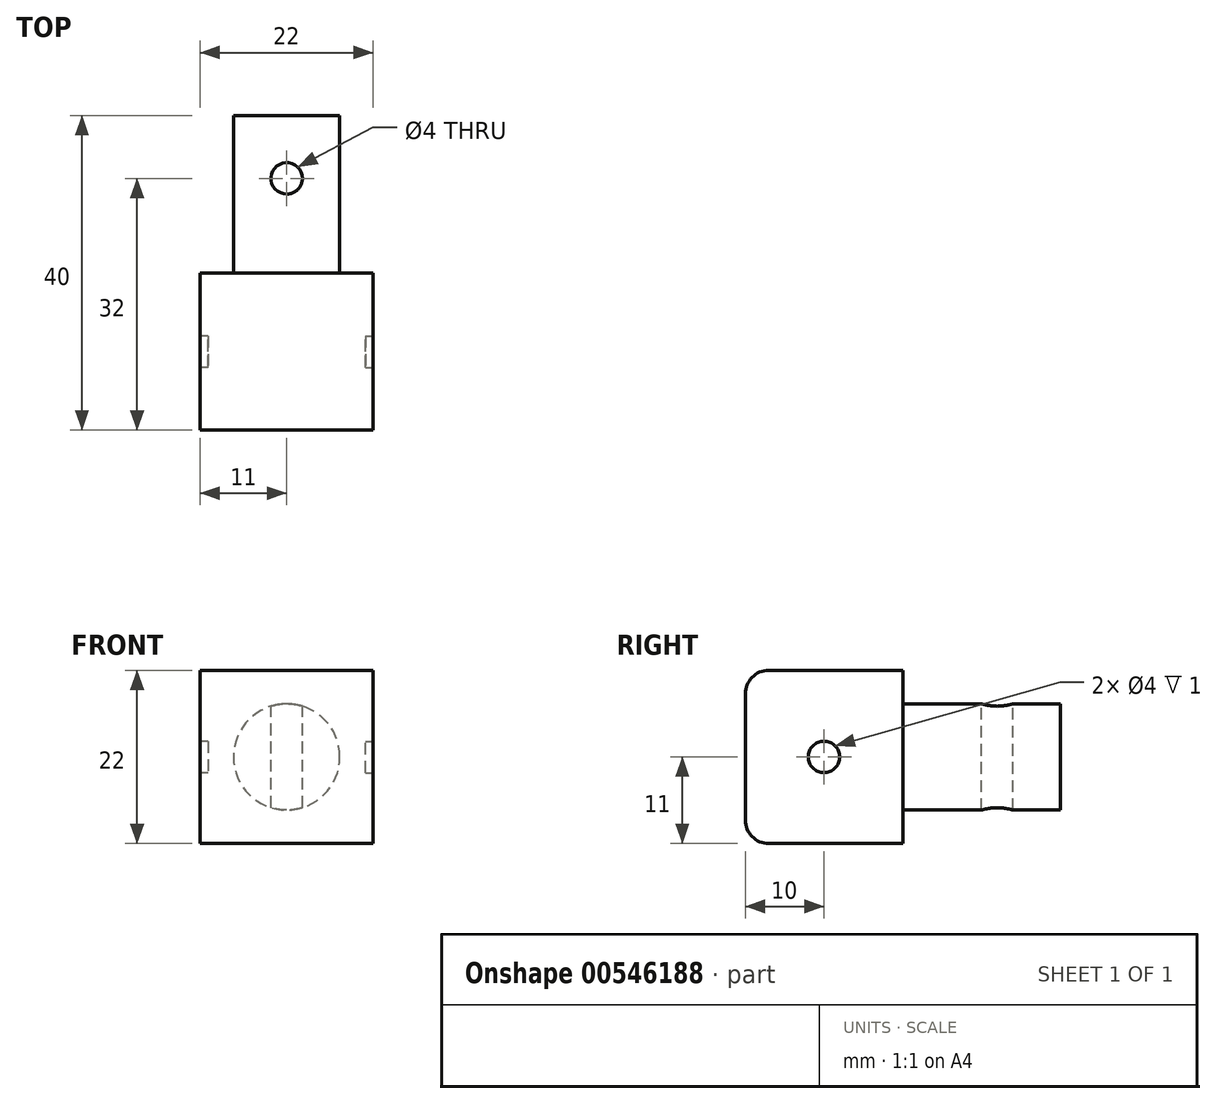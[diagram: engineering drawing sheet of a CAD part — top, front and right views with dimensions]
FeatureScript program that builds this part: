
annotation { "Feature Type Name" : "Feature", "Feature Type Description" : "" }
export const myFeature = defineFeature(function(context is Context, id is Id, definition is map)
    precondition{}
    {
        {
            var Q0;
            Q0=qCreatedBy(makeId("Front.planeOp"),FACE);
            var sketch = newSketch(context, id + "F0", { "sketchPlane" : qUnion([Q0])});
            skCircle(sketch, "E0", {"center": v(0, 0) * mm, "radius": 6.75 * mm});
            skSolve(sketch);
        }
        {
            var Q0;
            Q0 = qSketchRegion(id + "F0", true);
            extrude(context, id + "F1", {"entities" : qUnion([Q0]), "depth" : 20 * mm, "offsetDistance" : 25 * mm});
        }
        {
            var Q0;
            Q0=makeQuery(id+"F1.opExtrude","CAP_FACE",FACE,{"disambiguationData":[OSD([sQuery(id+"F0.wireOp",EDGE,"E0")])],"isStart":false});
            var sketch = newSketch(context, id + "F2", { "sketchPlane" : qUnion([Q0])});
            skLineSegment(sketch, "E1.bottom", {"start": v(-11, 11) * mm, "end": v(11, 11) * mm});
            skLineSegment(sketch, "E1.top", {"start": v(-11, -11) * mm, "end": v(11, -11) * mm});
            skLineSegment(sketch, "E1.left", {"start": v(-11, 11) * mm, "end": v(-11, -11) * mm});
            skLineSegment(sketch, "E1.right", {"start": v(11, 11) * mm, "end": v(11, -11) * mm});
            skPoint(sketch, "E1.middle", {"position": v(0, 0) * mm});
            skSolve(sketch);
        }
        {
            var Q0;
            Q0 = qSketchRegion(id + "F2", true);
            extrude(context, id + "F3", {"entities" : qUnion([Q0]), "operationType" : NewBodyOperationType.ADD, "depth" : 20 * mm, "offsetDistance" : 25 * mm});
        }
        {
            var Q0;
            Q0=makeQuery(id+"F3.opExtrude","CAP_EDGE",EDGE,{"disambiguationData":[OSD([sQuery(id+"F2.wireOp",EDGE,"E1.bottom")])],"isStart":false});
            var Q1;
            Q1=makeQuery(id+"F3.opExtrude","CAP_EDGE",EDGE,{"disambiguationData":[OSD([sQuery(id+"F2.wireOp",EDGE,"E1.top")])],"isStart":false});
            fillet(context, id + "F4", {"entities" : qUnion([Q0, Q1]), "radius" : 3 * mm, "tangentPropagation" : true, "allowEdgeOverflow" : false});
        }
        {
            var Q0;
            Q0=makeQuery(id+"F3.opExtrude","SWEPT_FACE",FACE,{"disambiguationData":[OSD([sQuery(id+"F2.wireOp",EDGE,"E1.right")])]});
            var sketch = newSketch(context, id + "F5", { "sketchPlane" : qUnion([Q0])});
            skLineSegment(sketch, "E2", {"start": v(-40, 0) * mm, "end": v(-30, 0) * mm});
            skPoint(sketch, "E2.endSnap0", {"position": v(-40, 0) * mm});
            skCircle(sketch, "E3", {"center": v(-30, 0) * mm, "radius": 2 * mm});
            skSolve(sketch);
        }
        {
            var Q0;
            Q0 = qSketchRegion(id + "F5", true);
            extrude(context, id + "F6", {"entities" : qUnion([Q0]), "operationType" : NewBodyOperationType.REMOVE, "oppositeDirection" : true, "depth" : 1 * mm, "offsetDistance" : 25 * mm});
        }
        {
            var Q0;
            Q0=makeQuery(id+"F3.opExtrude","SWEPT_FACE",FACE,{"disambiguationData":[OSD([sQuery(id+"F2.wireOp",EDGE,"E1.left")])]});
            var sketch = newSketch(context, id + "F7", { "sketchPlane" : qUnion([Q0])});
            skLineSegment(sketch, "E4", {"start": v(40, 0) * mm, "end": v(30, 0) * mm});
            skPoint(sketch, "E4.endSnap0", {"position": v(40, 0) * mm});
            skCircle(sketch, "E5", {"center": v(30, 0) * mm, "radius": 2 * mm});
            skSolve(sketch);
        }
        {
            var Q0;
            Q0 = qSketchRegion(id + "F7", true);
            extrude(context, id + "F8", {"entities" : qUnion([Q0]), "operationType" : NewBodyOperationType.REMOVE, "oppositeDirection" : true, "depth" : 1 * mm, "offsetDistance" : 25 * mm});
        }
        {
            var Q0;
            Q0=makeQuery(id+"F3.opExtrude","SWEPT_FACE",FACE,{"disambiguationData":[OSD([sQuery(id+"F2.wireOp",EDGE,"E1.bottom")])]});
            var sketch = newSketch(context, id + "F9", { "sketchPlane" : qUnion([Q0])});
            skLineSegment(sketch, "E6", {"start": v(0, -20) * mm, "end": v(0, -8) * mm});
            skCircle(sketch, "E7", {"center": v(0, -8) * mm, "radius": 2 * mm});
            skSolve(sketch);
        }
        {
            var Q0;
            Q0=makeQuery(id+"F9.imprint","IMPRINT",FACE,{"disambiguationData":[TD([[makeQuery(id+"F9.imprint","IMPRINT",EDGE,{"derivedFrom":sQuery(id+"F9.wireOp",EDGE,"E7")}),1.0]])]});
            extrude(context, id + "F10", {"entities" : qUnion([Q0]), "operationType" : NewBodyOperationType.REMOVE, "oppositeDirection" : true, "depth" : 25 * mm, "offsetDistance" : 25 * mm});
        }
    });
